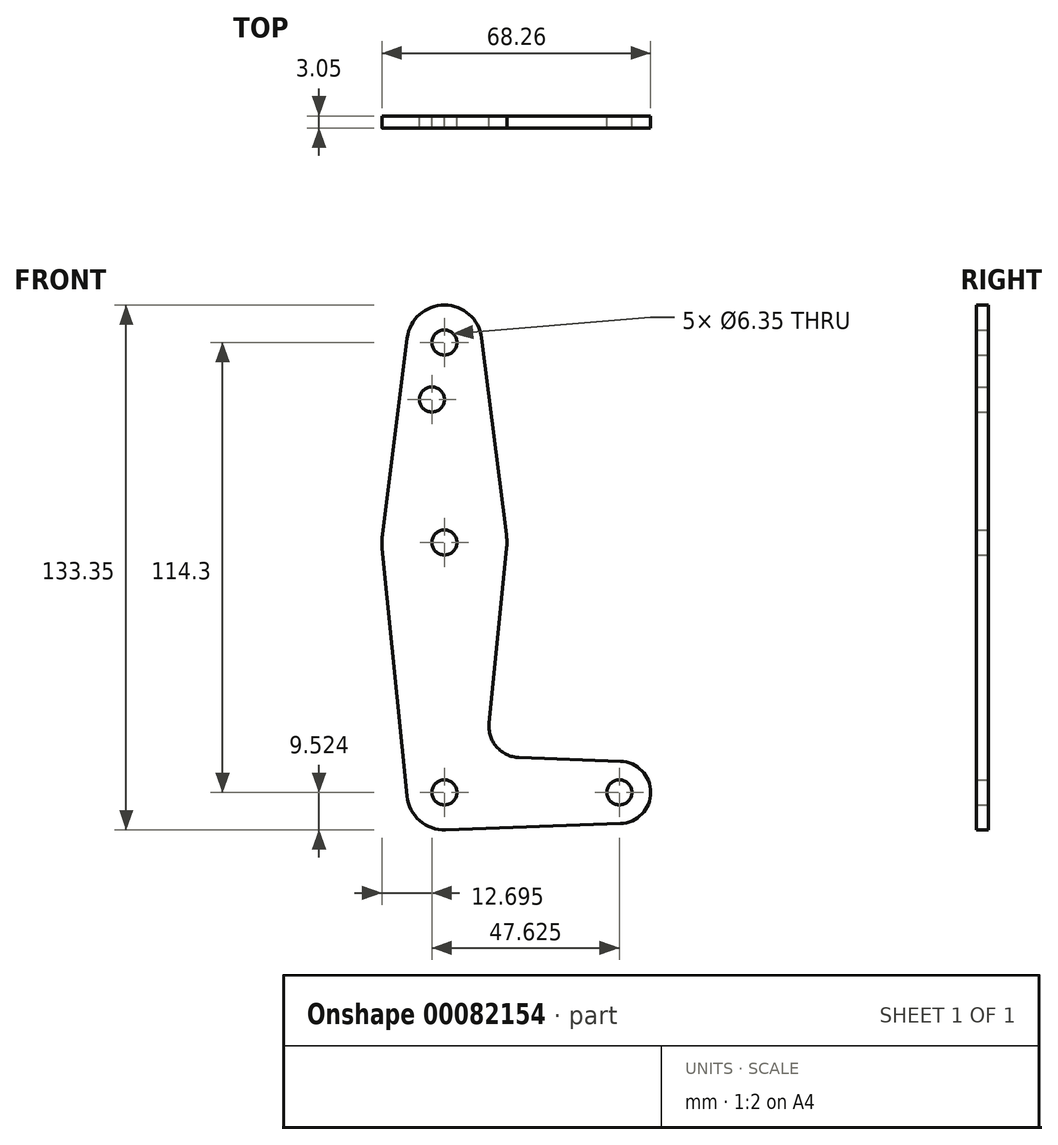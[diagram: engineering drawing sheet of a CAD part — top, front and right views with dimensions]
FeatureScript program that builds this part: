
annotation { "Feature Type Name" : "Feature", "Feature Type Description" : "" }
export const myFeature = defineFeature(function(context is Context, id is Id, definition is map)
    precondition{}
    {
        {
            var Q0;
            Q0=qCreatedBy(makeId("Front.planeOp"),FACE);
            var sketch = newSketch(context, id + "F0", { "sketchPlane" : qUnion([Q0])});
            skLineSegment(sketch, "E0", {"start": v(0, 69.9) * mm, "end": v(0, -44.4) * mm, "construction": true});
            skCircle(sketch, "E1", {"center": v(0, 69.9) * mm, "radius": 9.53 * mm});
            skCircle(sketch, "E2", {"center": v(0, -44.4) * mm, "radius": 9.53 * mm});
            skLineSegment(sketch, "E3", {"start": v(0, -44.4) * mm, "end": v(44.45, -44.4) * mm, "construction": true});
            skCircle(sketch, "E4", {"center": v(0, 19.1) * mm, "radius": 15.88 * mm});
            skCircle(sketch, "E5", {"center": v(44.45, -44.4) * mm, "radius": 7.94 * mm});
            skLineSegment(sketch, "E6", {"start": v(-9.45, 71.1) * mm, "end": v(-15.75, 21.09) * mm});
            skLineSegment(sketch, "E7", {"start": v(9.45, 71.1) * mm, "end": v(15.75, 21.09) * mm});
            skLineSegment(sketch, "E8", {"start": v(15.8, 17.52) * mm, "end": v(11.34, -26.8) * mm});
            skLineSegment(sketch, "E9", {"start": v(-15.8, 17.52) * mm, "end": v(-9.48, -45.35) * mm});
            skLineSegment(sketch, "E10", {"start": v(44.73, -36.46) * mm, "end": v(18.97, -35.54) * mm});
            skLineSegment(sketch, "E11", {"start": v(44.73, -52.33) * mm, "end": v(0.34, -53.91) * mm});
            skCircle(sketch, "E12", {"center": v(0, 69.9) * mm, "radius": 3.18 * mm});
            skCircle(sketch, "E13", {"center": v(0, 19.1) * mm, "radius": 3.18 * mm});
            skCircle(sketch, "E14", {"center": v(0, -44.4) * mm, "radius": 3.18 * mm});
            skCircle(sketch, "E15", {"center": v(44.45, -44.4) * mm, "radius": 3.18 * mm});
            skCircle(sketch, "E16", {"center": v(-3.17, 55.43) * mm, "radius": 3.18 * mm});
            skPoint(sketch, "E17.newPointA", {"position": v(9.57, -44.4) * mm});
            skArc(sketch, "E17.filletArc", {"start": v(11.34, -26.8) * mm, "mid": v(13.26, -32.82) * mm, "end": v(18.97, -35.54) * mm});
            skSolve(sketch);
        }
        {
            var Q0;
            Q0 = qSketchRegion(id + "F0", true);
            extrude(context, id + "F1", {"entities" : qUnion([Q0]), "depth" : 3.05 * mm});
        }
    });
